# Revit family: RN 15101 Valvola di ritegno EA
name_source: partatom
category: Rohrzubehör
units: mm (PartAtom-declared; Revit-internal decimal feet)

## family parameters
Arbeitsebenenbasiert = Nein
Beim Laden mit Abzugskörper schneiden = Nein
Bemaßung runder Anschluss = Durchmesser verwenden
Gemeinsam genutzt = Nein
Immer vertikal = Ja
Teiletyp = Ventil - Zerlegung in

## types (7) — shared parameters
1.010.00.2 Blattnummer der Richtlinie = 17
1.010.00.3 Ausgabedatum (Monat) der Richtlinie = 201601
1.010.00.4 Herstellername = R. Nussbaum AG
1.010.00.5 Revisionsdatum der Datei = 20190528
1.010.00.6 Webadresse des Herstellers = http://www.nussbaum.ch
1.100.00.3 Sortiernummer für Anzeigereihenfolge = 4
1.100.00.4 Produktbezeichnung = Sicherungs- und Ringleitungsarmaturen
1.960/3L.00.8 Link (URL) = https://www.nussbaum.ch
17.700.00.4 Armaturentyp = 6
17.700.00.7 Maximale Betriebstemperatur TB [°C] = 90
17.700.00.8 Maximaler Betriebsdruck (Arbeitsdruck) ps [1.0 · 105 Pa] = 16
Connector Visibility = Nein
EnclosingSpace Visibility = Nein
Hersteller = R. Nussbauzm AG
URL = https://www.nussbaum.ch

## per-type parameters (varying)
- DN 65: 1.800.00.3 TGA-Nummer=0040160000000000000000000000020070000000000000000100000000; 1.810.00.3 Hersteller-Bestellnummer=15101.1; 1.810.00.4 DATANORM-Nummer=15101.1; 1.810.00.5 StLB-Nummer=614.541; 1.810.00.6 GTIN-Nummer=7612945726308; 17.700.00.30 Produktbeschreibung=15101.10, Rückflussverhinderer EA, DN=65, Rp=2½; 17.700.00.5 Nennweite DN=65; 17.700.00.6 kvs-Wert [m3/h]=114; CONNECTOR0_DIAMETER_dX_0r=65 mm; CONNECTOR0_dX_00=92 mm; CONNECTOR0_dX_01=65 mm; CONNECTOR0_ref_dX=65 mm; CONNECTOR1_DIAMETER_dX_0r=65 mm; CONNECTOR1_dX_00=65 mm; CONNECTOR1_dX_01=92 mm; CONNECTOR1_ref_dX=65 mm; Modell=15101.1; R. Nussbaum AG 15101.04 de Visibility=Nein; R. Nussbaum AG 15101.05 de Visibility=Nein; R. Nussbaum AG 15101.06 de Visibility=Nein; R. Nussbaum AG 15101.07 de Visibility=Nein; R. Nussbaum AG 15101.08 de Visibility=Nein; R. Nussbaum AG 15101.09 de Visibility=Nein; R. Nussbaum AG 15101.10 de Visibility=Ja; Typenkommentare=Valvola di ritegno EADN 65
- DN 15: 1.800.00.3 TGA-Nummer=0040160000000000000000000000020070000000000000000200000000; 1.810.00.3 Hersteller-Bestellnummer=15101.04; 1.810.00.4 DATANORM-Nummer=15101.04; 1.810.00.5 StLB-Nummer=614.533; 1.810.00.6 GTIN-Nummer=7612945737007; 17.700.00.30 Produktbeschreibung=15101.04, Rückflussverhinderer EA, DN=15, Rp=½; 17.700.00.5 Nennweite DN=15; 17.700.00.6 kvs-Wert [m3/h]=5.4; CONNECTOR0_DIAMETER_dX_0r=15 mm  [stored 0.0492126 ft]; CONNECTOR0_dX_00=35 mm; CONNECTOR0_dX_01=22 mm; CONNECTOR0_ref_dX=22 mm; CONNECTOR1_DIAMETER_dX_0r=15 mm  [stored 0.0492126 ft]; CONNECTOR1_dX_00=22 mm; CONNECTOR1_dX_01=35 mm; CONNECTOR1_ref_dX=22 mm; Modell=15101.04; R. Nussbaum AG 15101.04 de Visibility=Ja; R. Nussbaum AG 15101.05 de Visibility=Nein; R. Nussbaum AG 15101.06 de Visibility=Nein; R. Nussbaum AG 15101.07 de Visibility=Nein; R. Nussbaum AG 15101.08 de Visibility=Nein; R. Nussbaum AG 15101.09 de Visibility=Nein; R. Nussbaum AG 15101.10 de Visibility=Nein; Typenkommentare=Valvola di ritegno EADN 15
- DN 20: 1.800.00.3 TGA-Nummer=0040160000000000000000000000020070000000000000000300000000; 1.810.00.3 Hersteller-Bestellnummer=15101.05; 1.810.00.4 DATANORM-Nummer=15101.05; 1.810.00.5 StLB-Nummer=614.534; 1.810.00.6 GTIN-Nummer=7612945737243; 17.700.00.30 Produktbeschreibung=15101.05, Rückflussverhinderer EA, DN=20, Rp=¾; 17.700.00.5 Nennweite DN=20; 17.700.00.6 kvs-Wert [m3/h]=10.8; CONNECTOR0_DIAMETER_dX_0r=20 mm; CONNECTOR0_dX_00=42 mm; CONNECTOR0_dX_01=27 mm; CONNECTOR0_ref_dX=27 mm; CONNECTOR1_DIAMETER_dX_0r=20 mm; CONNECTOR1_dX_00=28 mm; CONNECTOR1_dX_01=43 mm; CONNECTOR1_ref_dX=28 mm; Modell=15101.05; R. Nussbaum AG 15101.04 de Visibility=Nein; R. Nussbaum AG 15101.05 de Visibility=Ja; R. Nussbaum AG 15101.06 de Visibility=Nein; R. Nussbaum AG 15101.07 de Visibility=Nein; R. Nussbaum AG 15101.08 de Visibility=Nein; R. Nussbaum AG 15101.09 de Visibility=Nein; R. Nussbaum AG 15101.10 de Visibility=Nein; Typenkommentare=Valvola di ritegno EADN 20
- DN 25: 1.800.00.3 TGA-Nummer=0040160000000000000000000000020070000000000000000400000000; 1.810.00.3 Hersteller-Bestellnummer=15101.06; 1.810.00.4 DATANORM-Nummer=15101.06; 1.810.00.5 StLB-Nummer=614.535; 1.810.00.6 GTIN-Nummer=7612945737557; 17.700.00.30 Produktbeschreibung=15101.06, Rückflussverhinderer EA, DN=25, Rp=1; 17.700.00.5 Nennweite DN=25; 17.700.00.6 kvs-Wert [m3/h]=16.8; CONNECTOR0_DIAMETER_dX_0r=25 mm  [stored 0.082021 ft]; CONNECTOR0_dX_00=50 mm; CONNECTOR0_dX_01=33 mm; CONNECTOR0_ref_dX=33 mm; CONNECTOR1_DIAMETER_dX_0r=25 mm  [stored 0.082021 ft]; CONNECTOR1_dX_00=33 mm; CONNECTOR1_dX_01=50 mm; CONNECTOR1_ref_dX=33 mm; Modell=15101.06; R. Nussbaum AG 15101.04 de Visibility=Nein; R. Nussbaum AG 15101.05 de Visibility=Nein; R. Nussbaum AG 15101.06 de Visibility=Ja; R. Nussbaum AG 15101.07 de Visibility=Nein; R. Nussbaum AG 15101.08 de Visibility=Nein; R. Nussbaum AG 15101.09 de Visibility=Nein; R. Nussbaum AG 15101.10 de Visibility=Nein; Typenkommentare=Valvola di ritegno EADN 25
- DN 32: 1.800.00.3 TGA-Nummer=0040160000000000000000000000020070000000000000000500000000; 1.810.00.3 Hersteller-Bestellnummer=15101.07; 1.810.00.4 DATANORM-Nummer=15101.07; 1.810.00.5 StLB-Nummer=614.536; 1.810.00.6 GTIN-Nummer=7612945735164; 17.700.00.30 Produktbeschreibung=15101.07, Rückflussverhinderer EA, DN=32, Rp=1¼; 17.700.00.5 Nennweite DN=32; 17.700.00.6 kvs-Wert [m3/h]=31.2; CONNECTOR0_DIAMETER_dX_0r=32 mm; CONNECTOR0_dX_00=57 mm; CONNECTOR0_dX_01=38 mm; CONNECTOR0_ref_dX=38 mm; CONNECTOR1_DIAMETER_dX_0r=32 mm; CONNECTOR1_dX_00=39 mm; CONNECTOR1_dX_01=58 mm; CONNECTOR1_ref_dX=39 mm; Modell=15101.07; R. Nussbaum AG 15101.04 de Visibility=Nein; R. Nussbaum AG 15101.05 de Visibility=Nein; R. Nussbaum AG 15101.06 de Visibility=Nein; R. Nussbaum AG 15101.07 de Visibility=Ja; R. Nussbaum AG 15101.08 de Visibility=Nein; R. Nussbaum AG 15101.09 de Visibility=Nein; R. Nussbaum AG 15101.10 de Visibility=Nein; Typenkommentare=Valvola di ritegno EADN 32
- DN 40: 1.800.00.3 TGA-Nummer=0040160000000000000000000000020070000000000000000600000000; 1.810.00.3 Hersteller-Bestellnummer=15101.08; 1.810.00.4 DATANORM-Nummer=15101.08; 1.810.00.5 StLB-Nummer=614.537; 1.810.00.6 GTIN-Nummer=7612945733665; 17.700.00.30 Produktbeschreibung=15101.08, Rückflussverhinderer EA, DN=40, Rp=1½; 17.700.00.5 Nennweite DN=40; 17.700.00.6 kvs-Wert [m3/h]=45; CONNECTOR0_DIAMETER_dX_0r=40 mm; CONNECTOR0_dX_00=65 mm; CONNECTOR0_dX_01=46 mm; CONNECTOR0_ref_dX=46 mm; CONNECTOR1_DIAMETER_dX_0r=40 mm; CONNECTOR1_dX_00=46 mm; CONNECTOR1_dX_01=65 mm; CONNECTOR1_ref_dX=46 mm; Modell=15101.08; R. Nussbaum AG 15101.04 de Visibility=Nein; R. Nussbaum AG 15101.05 de Visibility=Nein; R. Nussbaum AG 15101.06 de Visibility=Nein; R. Nussbaum AG 15101.07 de Visibility=Nein; R. Nussbaum AG 15101.08 de Visibility=Ja; R. Nussbaum AG 15101.09 de Visibility=Nein; R. Nussbaum AG 15101.10 de Visibility=Nein; Typenkommentare=Valvola di ritegno EADN 40
- DN 50: 1.800.00.3 TGA-Nummer=0040160000000000000000000000020070000000000000000700000000; 1.810.00.3 Hersteller-Bestellnummer=15101.09; 1.810.00.4 DATANORM-Nummer=15101.09; 1.810.00.5 StLB-Nummer=614.538; 1.810.00.6 GTIN-Nummer=7612945733894; 17.700.00.30 Produktbeschreibung=15101.09, Rückflussverhinderer EA, DN=50, Rp=2; 17.700.00.5 Nennweite DN=50; 17.700.00.6 kvs-Wert [m3/h]=69; CONNECTOR0_DIAMETER_dX_0r=50 mm; CONNECTOR0_dX_00=75 mm; CONNECTOR0_dX_01=51 mm; CONNECTOR0_ref_dX=51 mm; CONNECTOR1_DIAMETER_dX_0r=50 mm; CONNECTOR1_dX_00=51 mm; CONNECTOR1_dX_01=75 mm; CONNECTOR1_ref_dX=51 mm; Modell=15101.09; R. Nussbaum AG 15101.04 de Visibility=Nein; R. Nussbaum AG 15101.05 de Visibility=Nein; R. Nussbaum AG 15101.06 de Visibility=Nein; R. Nussbaum AG 15101.07 de Visibility=Nein; R. Nussbaum AG 15101.08 de Visibility=Nein; R. Nussbaum AG 15101.09 de Visibility=Ja; R. Nussbaum AG 15101.10 de Visibility=Nein; Typenkommentare=Valvola di ritegno EADN 50

note: [stored X ft] marks values corroborated as IEEE doubles in the binary element streams (Revit-internal decimal feet)
